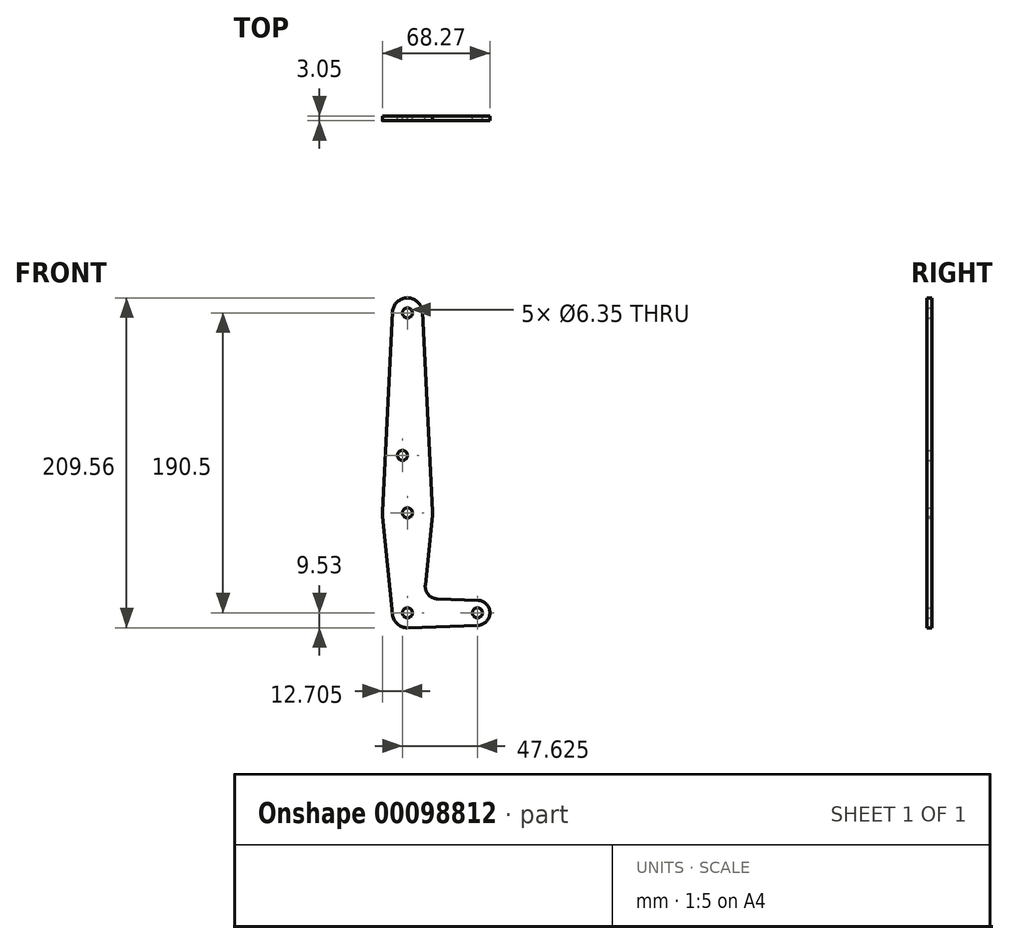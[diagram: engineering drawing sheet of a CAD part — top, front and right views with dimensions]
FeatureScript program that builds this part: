
annotation { "Feature Type Name" : "Feature", "Feature Type Description" : "" }
export const myFeature = defineFeature(function(context is Context, id is Id, definition is map)
    precondition{}
    {
        {
            var Q0;
            Q0=qCreatedBy(makeId("Front.planeOp"),FACE);
            var sketch = newSketch(context, id + "F0", { "sketchPlane" : qUnion([Q0])});
            skCircle(sketch, "E0", {"center": v(0, 0) * mm, "radius": 9.53 * mm});
            skCircle(sketch, "E1", {"center": v(0, 63.5) * mm, "radius": 15.88 * mm});
            skCircle(sketch, "E2", {"center": v(0, 190.5) * mm, "radius": 9.53 * mm});
            skCircle(sketch, "E3", {"center": v(44.45, 0) * mm, "radius": 7.94 * mm});
            skLineSegment(sketch, "E4", {"start": v(0, 190.5) * mm, "end": v(0, 0) * mm, "construction": true});
            skLineSegment(sketch, "E5", {"start": v(0, 0) * mm, "end": v(44.45, 0) * mm, "construction": true});
            skLineSegment(sketch, "E6", {"start": v(-15.86, 64.3) * mm, "end": v(-9.51, 190.98) * mm});
            skLineSegment(sketch, "E7", {"start": v(-15.86, 62.7) * mm, "end": v(-9.48, -0.95) * mm});
            skLineSegment(sketch, "E8", {"start": v(9.51, 190.98) * mm, "end": v(15.86, 64.3) * mm});
            skLineSegment(sketch, "E9", {"start": v(11.34, 17.6) * mm, "end": v(15.8, 61.91) * mm});
            skLineSegment(sketch, "E10", {"start": v(18.97, 8.85) * mm, "end": v(44.73, 7.93) * mm});
            skLineSegment(sketch, "E11", {"start": v(0.34, -9.52) * mm, "end": v(44.73, -7.93) * mm});
            skCircle(sketch, "E12", {"center": v(0, 190.5) * mm, "radius": 3.18 * mm});
            skCircle(sketch, "E13", {"center": v(0, 63.5) * mm, "radius": 3.18 * mm});
            skCircle(sketch, "E14", {"center": v(-3.17, 100.03) * mm, "radius": 3.18 * mm});
            skCircle(sketch, "E15", {"center": v(44.45, 0) * mm, "radius": 3.18 * mm});
            skCircle(sketch, "E16", {"center": v(0, 0) * mm, "radius": 3.18 * mm});
            skArc(sketch, "E17.filletArc", {"start": v(11.34, 17.6) * mm, "mid": v(13.26, 11.57) * mm, "end": v(18.97, 8.85) * mm});
            skSolve(sketch);
        }
        {
            var Q0;
            Q0 = qSketchRegion(id + "F0", true);
            extrude(context, id + "F1", {"entities" : qUnion([Q0]), "depth" : 3.05 * mm});
        }
    });
